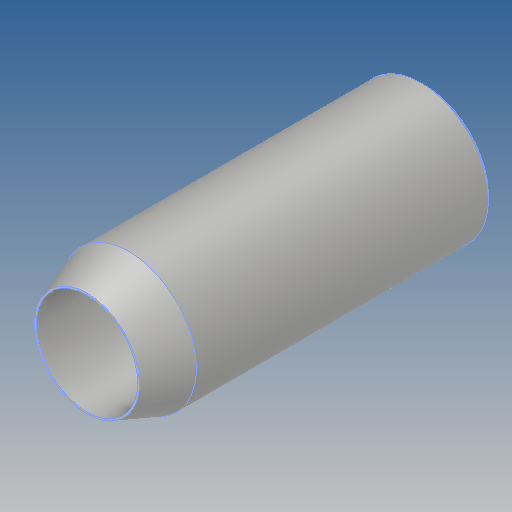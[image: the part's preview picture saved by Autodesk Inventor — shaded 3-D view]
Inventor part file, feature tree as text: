
AUTODESK INVENTOR PART (.ipt)
format: ipt  version: 2019 (Build 230136000, 136)  size: 132,608 bytes
history: native  units: mm
features: other x1, chamfer x1, sketch x1
ambient origin geometry x8: Origin, YZ Plane, XZ Plane, XY Plane, X Axis, Y Axis, Z Axis, Center Point
bodies: Solide1 (feature_tree)
feature tree (3):
  other  "Révolution1"
  chamfer  "Chanfrein1"  Distance=27.925268mm
  sketch  "Esquisse1"
